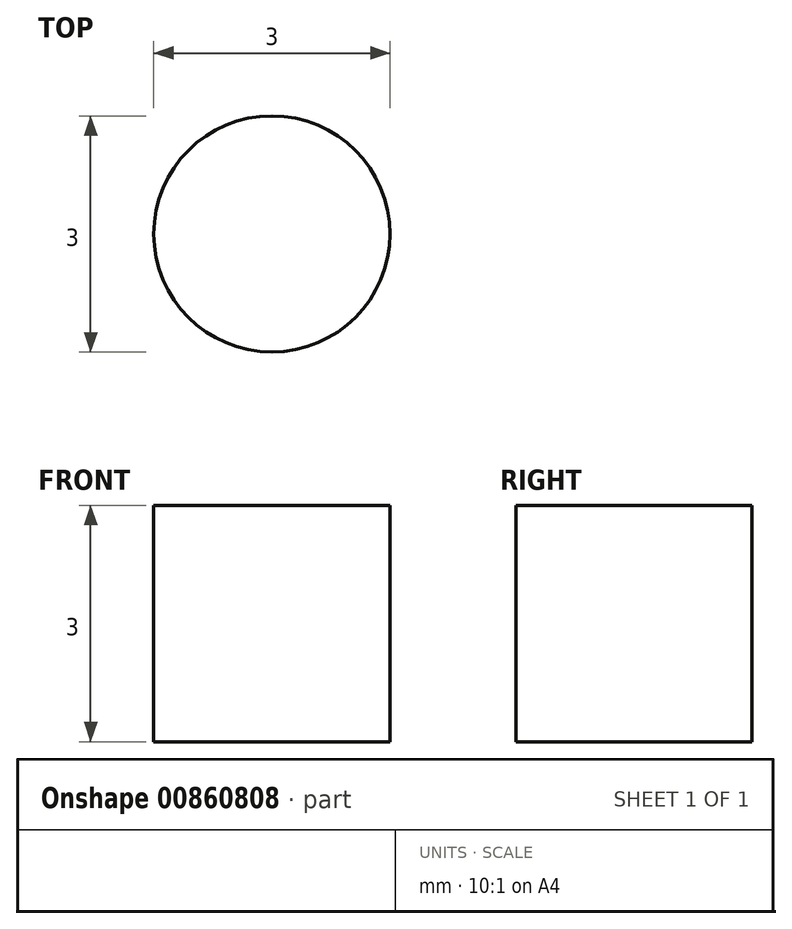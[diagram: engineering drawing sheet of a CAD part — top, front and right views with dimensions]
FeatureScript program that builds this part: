
annotation { "Feature Type Name" : "Feature", "Feature Type Description" : "" }
export const myFeature = defineFeature(function(context is Context, id is Id, definition is map)
    precondition{}
    {
        {
            var Q0;
            Q0=qCreatedBy(makeId("Top.planeOp"),FACE);
            var sketch = newSketch(context, id + "F0", { "sketchPlane" : qUnion([Q0])});
            skCircle(sketch, "E0", {"center": v(-15.25, 15.25) * mm, "radius": 1.5 * mm});
            skCircle(sketch, "E1", {"center": v(15.25, 15.25) * mm, "radius": 1.5 * mm});
            skCircle(sketch, "E2", {"center": v(-15.25, -15.25) * mm, "radius": 1.5 * mm});
            skCircle(sketch, "E3", {"center": v(15.25, -15.25) * mm, "radius": 1.5 * mm});
            skCircle(sketch, "E4", {"center": v(-12, 34.35) * mm, "radius": 1 * mm});
            skCircle(sketch, "E5", {"center": v(12, 34.35) * mm, "radius": 1 * mm});
            skCircle(sketch, "E6", {"center": v(-12, -26.35) * mm, "radius": 1 * mm});
            skCircle(sketch, "E7", {"center": v(-12, -34.35) * mm, "radius": 1 * mm});
            skCircle(sketch, "E8", {"center": v(12, -26.35) * mm, "radius": 1 * mm});
            skCircle(sketch, "E9", {"center": v(12, -34.35) * mm, "radius": 1 * mm});
            skCircle(sketch, "E10", {"center": v(-12, 26.35) * mm, "radius": 1 * mm});
            skCircle(sketch, "E11", {"center": v(12, 26.35) * mm, "radius": 1 * mm});
            skArc(sketch, "E12", {"start": v(9.25, 7) * mm, "mid": v(10.66, 6.41) * mm, "end": v(11.25, 5) * mm});
            skLineSegment(sketch, "E13", {"start": v(11.25, 5) * mm, "end": v(11.25, -5) * mm});
            skArc(sketch, "E14", {"start": v(11.25, -5) * mm, "mid": v(10.66, -6.41) * mm, "end": v(9.25, -7) * mm});
            skLineSegment(sketch, "E15", {"start": v(9.25, -7) * mm, "end": v(-9.25, -7) * mm});
            skArc(sketch, "E16", {"start": v(-9.25, -7) * mm, "mid": v(-10.66, -6.41) * mm, "end": v(-11.25, -5) * mm});
            skLineSegment(sketch, "E17", {"start": v(-11.25, -5) * mm, "end": v(-11.25, 5) * mm});
            skArc(sketch, "E18", {"start": v(-11.25, 5) * mm, "mid": v(-10.66, 6.41) * mm, "end": v(-9.25, 7) * mm});
            skLineSegment(sketch, "E19", {"start": v(-9.25, 7) * mm, "end": v(9.25, 7) * mm});
            skArc(sketch, "E20", {"start": v(8.75, 20.38) * mm, "mid": v(7.87, 18.26) * mm, "end": v(5.75, 17.38) * mm});
            skLineSegment(sketch, "E21", {"start": v(5.75, 17.38) * mm, "end": v(-5.75, 17.38) * mm});
            skArc(sketch, "E22", {"start": v(-5.75, 17.38) * mm, "mid": v(-7.87, 18.26) * mm, "end": v(-8.75, 20.38) * mm});
            skLineSegment(sketch, "E23", {"start": v(-8.75, 20.38) * mm, "end": v(-8.75, 30.5) * mm});
            skArc(sketch, "E24", {"start": v(-8.75, 30.5) * mm, "mid": v(-7.87, 32.62) * mm, "end": v(-5.75, 33.5) * mm});
            skLineSegment(sketch, "E25", {"start": v(-5.75, 33.5) * mm, "end": v(5.75, 33.5) * mm});
            skArc(sketch, "E26", {"start": v(5.75, 33.5) * mm, "mid": v(7.87, 32.62) * mm, "end": v(8.75, 30.5) * mm});
            skLineSegment(sketch, "E27", {"start": v(8.75, 30.5) * mm, "end": v(8.75, 20.38) * mm});
            skArc(sketch, "E28", {"start": v(-8.75, -30.74) * mm, "mid": v(-7.87, -32.86) * mm, "end": v(-5.75, -33.74) * mm});
            skLineSegment(sketch, "E29", {"start": v(-5.75, -33.74) * mm, "end": v(5.75, -33.74) * mm});
            skArc(sketch, "E30", {"start": v(5.75, -33.74) * mm, "mid": v(7.87, -32.86) * mm, "end": v(8.75, -30.74) * mm});
            skLineSegment(sketch, "E31", {"start": v(8.75, -30.74) * mm, "end": v(8.75, -20.38) * mm});
            skArc(sketch, "E32", {"start": v(8.75, -20.38) * mm, "mid": v(7.87, -18.26) * mm, "end": v(5.75, -17.38) * mm});
            skLineSegment(sketch, "E33", {"start": v(5.75, -17.38) * mm, "end": v(-5.75, -17.38) * mm});
            skArc(sketch, "E34", {"start": v(-5.75, -17.38) * mm, "mid": v(-7.87, -18.26) * mm, "end": v(-8.75, -20.38) * mm});
            skLineSegment(sketch, "E35", {"start": v(-8.75, -20.38) * mm, "end": v(-8.75, -30.74) * mm});
            skArc(sketch, "E36", {"start": v(39.96, 38.59) * mm, "mid": v(43.69, 41.27) * mm, "end": v(46.43, 44.96) * mm});
            skArc(sketch, "E37", {"start": v(46.43, 44.96) * mm, "mid": v(47.84, 47.05) * mm, "end": v(49.68, 48.78) * mm});
            skLineSegment(sketch, "E38", {"start": v(49.68, 48.78) * mm, "end": v(53.4, 51.6) * mm});
            skArc(sketch, "E39", {"start": v(53.4, 51.6) * mm, "mid": v(54.77, 52.32) * mm, "end": v(56.3, 52.6) * mm});
            skArc(sketch, "E40", {"start": v(56.3, 52.6) * mm, "mid": v(56.85, 52.6) * mm, "end": v(57.4, 52.58) * mm});
            skArc(sketch, "E41", {"start": v(57.4, 52.58) * mm, "mid": v(57.63, 52.62) * mm, "end": v(57.82, 52.76) * mm});
            skArc(sketch, "E42", {"start": v(57.82, 52.76) * mm, "mid": v(58, 52.9) * mm, "end": v(58.23, 52.94) * mm});
            skArc(sketch, "E43", {"start": v(58.23, 52.94) * mm, "mid": v(59, 52.87) * mm, "end": v(59.75, 52.73) * mm});
            skArc(sketch, "E44", {"start": v(59.75, 52.73) * mm, "mid": v(61.9, 52.01) * mm, "end": v(63.91, 50.95) * mm});
            skArc(sketch, "E45", {"start": v(63.91, 50.95) * mm, "mid": v(64.09, 50.75) * mm, "end": v(64.14, 50.49) * mm});
            skArc(sketch, "E46", {"start": v(64.14, 50.49) * mm, "mid": v(64.18, 50.24) * mm, "end": v(64.34, 50.04) * mm});
            skArc(sketch, "E47", {"start": v(64.34, 50.04) * mm, "mid": v(65.38, 49.18) * mm, "end": v(66.33, 48.22) * mm});
            skArc(sketch, "E48", {"start": v(66.33, 48.22) * mm, "mid": v(66.54, 48.08) * mm, "end": v(66.79, 48.06) * mm});
            skArc(sketch, "E49", {"start": v(66.79, 48.06) * mm, "mid": v(67.05, 48.03) * mm, "end": v(67.27, 47.87) * mm});
            skArc(sketch, "E50", {"start": v(67.27, 47.87) * mm, "mid": v(68.84, 45.3) * mm, "end": v(69.8, 42.45) * mm});
            skArc(sketch, "E51", {"start": v(69.8, 42.45) * mm, "mid": v(69.78, 42.19) * mm, "end": v(69.63, 41.97) * mm});
            skArc(sketch, "E52", {"start": v(69.63, 41.97) * mm, "mid": v(69.49, 41.76) * mm, "end": v(69.46, 41.51) * mm});
            skArc(sketch, "E53", {"start": v(69.46, 41.51) * mm, "mid": v(69.59, 40.17) * mm, "end": v(69.58, 38.82) * mm});
            skArc(sketch, "E54", {"start": v(69.58, 38.82) * mm, "mid": v(69.62, 38.57) * mm, "end": v(69.79, 38.38) * mm});
            skArc(sketch, "E55", {"start": v(69.79, 38.38) * mm, "mid": v(69.96, 38.17) * mm, "end": v(70, 37.9) * mm});
            skArc(sketch, "E56", {"start": v(70, 37.9) * mm, "mid": v(69.65, 36.14) * mm, "end": v(69.07, 34.43) * mm});
            skArc(sketch, "E57", {"start": v(69.07, 34.43) * mm, "mid": v(68.5, 33.3) * mm, "end": v(67.75, 32.28) * mm});
            skArc(sketch, "E58", {"start": v(67.75, 32.28) * mm, "mid": v(67.6, 32.16) * mm, "end": v(67.42, 32.1) * mm});
            skArc(sketch, "E59", {"start": v(67.42, 32.1) * mm, "mid": v(67.23, 32.04) * mm, "end": v(67.08, 31.9) * mm});
            skArc(sketch, "E60", {"start": v(67.08, 31.9) * mm, "mid": v(67, 31.8) * mm, "end": v(66.94, 31.71) * mm});
            skArc(sketch, "E61", {"start": v(66.94, 31.71) * mm, "mid": v(65.82, 30.64) * mm, "end": v(64.42, 29.97) * mm});
            skLineSegment(sketch, "E62", {"start": v(64.42, 29.97) * mm, "end": v(59.96, 28.6) * mm});
            skArc(sketch, "E63", {"start": v(59.96, 28.6) * mm, "mid": v(57.48, 28.13) * mm, "end": v(54.96, 28.22) * mm});
            skArc(sketch, "E64", {"start": v(54.96, 28.22) * mm, "mid": v(50.37, 28.17) * mm, "end": v(46, 26.74) * mm});
            skLineSegment(sketch, "E65", {"start": v(46, 26.74) * mm, "end": v(23.16, 15.1) * mm});
            skArc(sketch, "E66", {"start": v(23.16, 15.1) * mm, "mid": v(19.58, 11.78) * mm, "end": v(18.25, 7.08) * mm});
            skLineSegment(sketch, "E67", {"start": v(18.25, 7.08) * mm, "end": v(18.25, -7.08) * mm});
            skArc(sketch, "E68", {"start": v(18.25, -7.08) * mm, "mid": v(19.58, -11.78) * mm, "end": v(23.16, -15.1) * mm});
            skLineSegment(sketch, "E69", {"start": v(23.16, -15.1) * mm, "end": v(46, -26.74) * mm});
            skArc(sketch, "E70", {"start": v(46, -26.74) * mm, "mid": v(50.37, -28.17) * mm, "end": v(54.96, -28.22) * mm});
            skArc(sketch, "E71", {"start": v(54.96, -28.22) * mm, "mid": v(57.48, -28.13) * mm, "end": v(59.96, -28.6) * mm});
            skLineSegment(sketch, "E72", {"start": v(59.96, -28.6) * mm, "end": v(64.42, -29.97) * mm});
            skArc(sketch, "E73", {"start": v(64.42, -29.97) * mm, "mid": v(65.82, -30.64) * mm, "end": v(66.94, -31.71) * mm});
            skArc(sketch, "E74", {"start": v(66.94, -31.71) * mm, "mid": v(67, -31.8) * mm, "end": v(67.08, -31.9) * mm});
            skArc(sketch, "E75", {"start": v(67.08, -31.9) * mm, "mid": v(67.23, -32.04) * mm, "end": v(67.42, -32.1) * mm});
            skArc(sketch, "E76", {"start": v(67.42, -32.1) * mm, "mid": v(67.6, -32.16) * mm, "end": v(67.75, -32.28) * mm});
            skArc(sketch, "E77", {"start": v(67.75, -32.28) * mm, "mid": v(68.5, -33.3) * mm, "end": v(69.07, -34.43) * mm});
            skArc(sketch, "E78", {"start": v(69.07, -34.43) * mm, "mid": v(69.65, -36.14) * mm, "end": v(70, -37.9) * mm});
            skArc(sketch, "E79", {"start": v(70, -37.9) * mm, "mid": v(69.96, -38.17) * mm, "end": v(69.79, -38.38) * mm});
            skArc(sketch, "E80", {"start": v(69.79, -38.38) * mm, "mid": v(69.62, -38.57) * mm, "end": v(69.58, -38.82) * mm});
            skArc(sketch, "E81", {"start": v(69.58, -38.82) * mm, "mid": v(69.59, -40.17) * mm, "end": v(69.46, -41.51) * mm});
            skArc(sketch, "E82", {"start": v(69.46, -41.51) * mm, "mid": v(69.49, -41.76) * mm, "end": v(69.63, -41.97) * mm});
            skArc(sketch, "E83", {"start": v(69.63, -41.97) * mm, "mid": v(69.78, -42.19) * mm, "end": v(69.8, -42.45) * mm});
            skArc(sketch, "E84", {"start": v(69.8, -42.45) * mm, "mid": v(68.84, -45.3) * mm, "end": v(67.27, -47.87) * mm});
            skArc(sketch, "E85", {"start": v(67.27, -47.87) * mm, "mid": v(67.05, -48.03) * mm, "end": v(66.79, -48.06) * mm});
            skArc(sketch, "E86", {"start": v(66.79, -48.06) * mm, "mid": v(66.54, -48.08) * mm, "end": v(66.33, -48.22) * mm});
            skArc(sketch, "E87", {"start": v(66.33, -48.22) * mm, "mid": v(65.38, -49.18) * mm, "end": v(64.34, -50.04) * mm});
            skArc(sketch, "E88", {"start": v(64.34, -50.04) * mm, "mid": v(64.18, -50.24) * mm, "end": v(64.14, -50.49) * mm});
            skArc(sketch, "E89", {"start": v(64.14, -50.49) * mm, "mid": v(64.09, -50.75) * mm, "end": v(63.91, -50.95) * mm});
            skArc(sketch, "E90", {"start": v(63.91, -50.95) * mm, "mid": v(61.9, -52.01) * mm, "end": v(59.75, -52.73) * mm});
            skArc(sketch, "E91", {"start": v(59.75, -52.73) * mm, "mid": v(59, -52.87) * mm, "end": v(58.23, -52.94) * mm});
            skArc(sketch, "E92", {"start": v(58.23, -52.94) * mm, "mid": v(58, -52.9) * mm, "end": v(57.82, -52.76) * mm});
            skArc(sketch, "E93", {"start": v(57.82, -52.76) * mm, "mid": v(57.63, -52.62) * mm, "end": v(57.4, -52.58) * mm});
            skArc(sketch, "E94", {"start": v(57.4, -52.58) * mm, "mid": v(56.85, -52.6) * mm, "end": v(56.3, -52.6) * mm});
            skArc(sketch, "E95", {"start": v(56.3, -52.6) * mm, "mid": v(54.77, -52.32) * mm, "end": v(53.4, -51.6) * mm});
            skLineSegment(sketch, "E96", {"start": v(53.4, -51.6) * mm, "end": v(49.68, -48.78) * mm});
            skArc(sketch, "E97", {"start": v(49.68, -48.78) * mm, "mid": v(47.84, -47.05) * mm, "end": v(46.43, -44.96) * mm});
            skArc(sketch, "E98", {"start": v(46.43, -44.96) * mm, "mid": v(43.69, -41.27) * mm, "end": v(39.96, -38.59) * mm});
            skLineSegment(sketch, "E99", {"start": v(39.96, -38.59) * mm, "end": v(24.22, -30.57) * mm});
            skArc(sketch, "E100", {"start": v(24.22, -30.57) * mm, "mid": v(18.37, -30.8) * mm, "end": v(15.5, -35.91) * mm});
            skLineSegment(sketch, "E101", {"start": v(15.5, -35.91) * mm, "end": v(15.5, -40.74) * mm});
            skLineSegment(sketch, "E102", {"start": v(15.5, -40.74) * mm, "end": v(-15.5, -40.74) * mm});
            skLineSegment(sketch, "E103", {"start": v(-15.5, -40.74) * mm, "end": v(-15.5, -35.91) * mm});
            skArc(sketch, "E104", {"start": v(-15.5, -35.91) * mm, "mid": v(-18.37, -30.8) * mm, "end": v(-24.22, -30.57) * mm});
            skLineSegment(sketch, "E105", {"start": v(-24.22, -30.57) * mm, "end": v(-39.96, -38.59) * mm});
            skArc(sketch, "E106", {"start": v(-39.96, -38.59) * mm, "mid": v(-43.69, -41.27) * mm, "end": v(-46.43, -44.96) * mm});
            skArc(sketch, "E107", {"start": v(-46.43, -44.96) * mm, "mid": v(-47.84, -47.05) * mm, "end": v(-49.68, -48.78) * mm});
            skLineSegment(sketch, "E108", {"start": v(-49.68, -48.78) * mm, "end": v(-53.4, -51.6) * mm});
            skArc(sketch, "E109", {"start": v(-53.4, -51.6) * mm, "mid": v(-54.77, -52.32) * mm, "end": v(-56.3, -52.6) * mm});
            skArc(sketch, "E110", {"start": v(-56.3, -52.6) * mm, "mid": v(-56.85, -52.6) * mm, "end": v(-57.4, -52.58) * mm});
            skArc(sketch, "E111", {"start": v(-57.4, -52.58) * mm, "mid": v(-57.63, -52.62) * mm, "end": v(-57.82, -52.76) * mm});
            skArc(sketch, "E112", {"start": v(-57.82, -52.76) * mm, "mid": v(-58, -52.9) * mm, "end": v(-58.23, -52.94) * mm});
            skArc(sketch, "E113", {"start": v(-58.23, -52.94) * mm, "mid": v(-59, -52.87) * mm, "end": v(-59.75, -52.73) * mm});
            skArc(sketch, "E114", {"start": v(-59.75, -52.73) * mm, "mid": v(-61.9, -52.01) * mm, "end": v(-63.91, -50.95) * mm});
            skArc(sketch, "E115", {"start": v(-63.91, -50.95) * mm, "mid": v(-64.09, -50.75) * mm, "end": v(-64.14, -50.49) * mm});
            skArc(sketch, "E116", {"start": v(-64.14, -50.49) * mm, "mid": v(-64.18, -50.24) * mm, "end": v(-64.34, -50.04) * mm});
            skArc(sketch, "E117", {"start": v(-64.34, -50.04) * mm, "mid": v(-65.38, -49.18) * mm, "end": v(-66.33, -48.22) * mm});
            skArc(sketch, "E118", {"start": v(-66.33, -48.22) * mm, "mid": v(-66.54, -48.08) * mm, "end": v(-66.79, -48.06) * mm});
            skArc(sketch, "E119", {"start": v(-66.79, -48.06) * mm, "mid": v(-67.05, -48.03) * mm, "end": v(-67.27, -47.87) * mm});
            skArc(sketch, "E120", {"start": v(-67.27, -47.87) * mm, "mid": v(-68.84, -45.3) * mm, "end": v(-69.8, -42.45) * mm});
            skArc(sketch, "E121", {"start": v(-69.8, -42.45) * mm, "mid": v(-69.78, -42.19) * mm, "end": v(-69.63, -41.97) * mm});
            skArc(sketch, "E122", {"start": v(-69.63, -41.97) * mm, "mid": v(-69.49, -41.76) * mm, "end": v(-69.46, -41.51) * mm});
            skArc(sketch, "E123", {"start": v(-69.46, -41.51) * mm, "mid": v(-69.59, -40.17) * mm, "end": v(-69.58, -38.82) * mm});
            skArc(sketch, "E124", {"start": v(-69.58, -38.82) * mm, "mid": v(-69.62, -38.57) * mm, "end": v(-69.79, -38.38) * mm});
            skArc(sketch, "E125", {"start": v(-69.79, -38.38) * mm, "mid": v(-69.96, -38.17) * mm, "end": v(-70, -37.9) * mm});
            skArc(sketch, "E126", {"start": v(-70, -37.9) * mm, "mid": v(-69.65, -36.14) * mm, "end": v(-69.07, -34.43) * mm});
            skArc(sketch, "E127", {"start": v(-69.07, -34.43) * mm, "mid": v(-68.5, -33.3) * mm, "end": v(-67.75, -32.28) * mm});
            skArc(sketch, "E128", {"start": v(-67.75, -32.28) * mm, "mid": v(-67.6, -32.16) * mm, "end": v(-67.42, -32.1) * mm});
            skArc(sketch, "E129", {"start": v(-67.42, -32.1) * mm, "mid": v(-67.23, -32.04) * mm, "end": v(-67.08, -31.9) * mm});
            skArc(sketch, "E130", {"start": v(-67.08, -31.9) * mm, "mid": v(-67, -31.8) * mm, "end": v(-66.94, -31.71) * mm});
            skArc(sketch, "E131", {"start": v(-66.94, -31.71) * mm, "mid": v(-65.82, -30.64) * mm, "end": v(-64.42, -29.97) * mm});
            skLineSegment(sketch, "E132", {"start": v(-64.42, -29.97) * mm, "end": v(-59.96, -28.6) * mm});
            skArc(sketch, "E133", {"start": v(-59.96, -28.6) * mm, "mid": v(-57.48, -28.13) * mm, "end": v(-54.96, -28.22) * mm});
            skArc(sketch, "E134", {"start": v(-54.96, -28.22) * mm, "mid": v(-50.37, -28.17) * mm, "end": v(-46, -26.74) * mm});
            skLineSegment(sketch, "E135", {"start": v(-46, -26.74) * mm, "end": v(-23.16, -15.1) * mm});
            skArc(sketch, "E136", {"start": v(-23.16, -15.1) * mm, "mid": v(-19.58, -11.78) * mm, "end": v(-18.25, -7.08) * mm});
            skLineSegment(sketch, "E137", {"start": v(-18.25, -7.08) * mm, "end": v(-18.25, 7.08) * mm});
            skArc(sketch, "E138", {"start": v(-18.25, 7.08) * mm, "mid": v(-19.58, 11.78) * mm, "end": v(-23.16, 15.1) * mm});
            skLineSegment(sketch, "E139", {"start": v(-23.16, 15.1) * mm, "end": v(-46, 26.74) * mm});
            skArc(sketch, "E140", {"start": v(-46, 26.74) * mm, "mid": v(-50.37, 28.17) * mm, "end": v(-54.96, 28.22) * mm});
            skArc(sketch, "E141", {"start": v(-54.96, 28.22) * mm, "mid": v(-57.48, 28.13) * mm, "end": v(-59.96, 28.6) * mm});
            skLineSegment(sketch, "E142", {"start": v(-59.96, 28.6) * mm, "end": v(-64.42, 29.97) * mm});
            skArc(sketch, "E143", {"start": v(-64.42, 29.97) * mm, "mid": v(-65.82, 30.64) * mm, "end": v(-66.94, 31.71) * mm});
            skArc(sketch, "E144", {"start": v(-66.94, 31.71) * mm, "mid": v(-67, 31.8) * mm, "end": v(-67.08, 31.9) * mm});
            skArc(sketch, "E145", {"start": v(-67.08, 31.9) * mm, "mid": v(-67.23, 32.04) * mm, "end": v(-67.42, 32.1) * mm});
            skArc(sketch, "E146", {"start": v(-67.42, 32.1) * mm, "mid": v(-67.6, 32.16) * mm, "end": v(-67.75, 32.28) * mm});
            skArc(sketch, "E147", {"start": v(-67.75, 32.28) * mm, "mid": v(-68.5, 33.3) * mm, "end": v(-69.07, 34.43) * mm});
            skArc(sketch, "E148", {"start": v(-69.07, 34.43) * mm, "mid": v(-69.65, 36.14) * mm, "end": v(-70, 37.9) * mm});
            skArc(sketch, "E149", {"start": v(-70, 37.9) * mm, "mid": v(-69.96, 38.17) * mm, "end": v(-69.79, 38.38) * mm});
            skArc(sketch, "E150", {"start": v(-69.79, 38.38) * mm, "mid": v(-69.62, 38.57) * mm, "end": v(-69.58, 38.82) * mm});
            skArc(sketch, "E151", {"start": v(-69.58, 38.82) * mm, "mid": v(-69.59, 40.17) * mm, "end": v(-69.46, 41.51) * mm});
            skArc(sketch, "E152", {"start": v(-69.46, 41.51) * mm, "mid": v(-69.49, 41.76) * mm, "end": v(-69.63, 41.97) * mm});
            skArc(sketch, "E153", {"start": v(-69.63, 41.97) * mm, "mid": v(-69.78, 42.19) * mm, "end": v(-69.8, 42.45) * mm});
            skArc(sketch, "E154", {"start": v(-69.8, 42.45) * mm, "mid": v(-68.84, 45.3) * mm, "end": v(-67.27, 47.87) * mm});
            skArc(sketch, "E155", {"start": v(-67.27, 47.87) * mm, "mid": v(-67.05, 48.03) * mm, "end": v(-66.79, 48.06) * mm});
            skArc(sketch, "E156", {"start": v(-66.79, 48.06) * mm, "mid": v(-66.54, 48.08) * mm, "end": v(-66.33, 48.22) * mm});
            skArc(sketch, "E157", {"start": v(-66.33, 48.22) * mm, "mid": v(-65.38, 49.18) * mm, "end": v(-64.34, 50.04) * mm});
            skArc(sketch, "E158", {"start": v(-64.34, 50.04) * mm, "mid": v(-64.18, 50.24) * mm, "end": v(-64.14, 50.49) * mm});
            skArc(sketch, "E159", {"start": v(-64.14, 50.49) * mm, "mid": v(-64.09, 50.75) * mm, "end": v(-63.91, 50.95) * mm});
            skArc(sketch, "E160", {"start": v(-63.91, 50.95) * mm, "mid": v(-61.9, 52.01) * mm, "end": v(-59.75, 52.73) * mm});
            skArc(sketch, "E161", {"start": v(-59.75, 52.73) * mm, "mid": v(-59, 52.87) * mm, "end": v(-58.23, 52.94) * mm});
            skArc(sketch, "E162", {"start": v(-58.23, 52.94) * mm, "mid": v(-58, 52.9) * mm, "end": v(-57.82, 52.76) * mm});
            skArc(sketch, "E163", {"start": v(-57.82, 52.76) * mm, "mid": v(-57.63, 52.62) * mm, "end": v(-57.4, 52.58) * mm});
            skArc(sketch, "E164", {"start": v(-57.4, 52.58) * mm, "mid": v(-56.85, 52.6) * mm, "end": v(-56.3, 52.6) * mm});
            skArc(sketch, "E165", {"start": v(-56.3, 52.6) * mm, "mid": v(-54.77, 52.32) * mm, "end": v(-53.4, 51.6) * mm});
            skLineSegment(sketch, "E166", {"start": v(-53.4, 51.6) * mm, "end": v(-49.68, 48.78) * mm});
            skArc(sketch, "E167", {"start": v(-49.68, 48.78) * mm, "mid": v(-47.84, 47.05) * mm, "end": v(-46.43, 44.96) * mm});
            skArc(sketch, "E168", {"start": v(-46.43, 44.96) * mm, "mid": v(-43.69, 41.27) * mm, "end": v(-39.96, 38.59) * mm});
            skLineSegment(sketch, "E169", {"start": v(-39.96, 38.59) * mm, "end": v(-24.22, 30.57) * mm});
            skArc(sketch, "E170", {"start": v(-24.22, 30.57) * mm, "mid": v(-18.37, 30.8) * mm, "end": v(-15.5, 35.91) * mm});
            skLineSegment(sketch, "E171", {"start": v(-15.5, 35.91) * mm, "end": v(-15.5, 37.85) * mm});
            skLineSegment(sketch, "E172", {"start": v(-15.5, 37.85) * mm, "end": v(15.5, 37.85) * mm});
            skLineSegment(sketch, "E173", {"start": v(15.5, 37.85) * mm, "end": v(15.5, 35.91) * mm});
            skArc(sketch, "E174", {"start": v(15.5, 35.91) * mm, "mid": v(18.37, 30.8) * mm, "end": v(24.22, 30.57) * mm});
            skLineSegment(sketch, "E175", {"start": v(24.22, 30.57) * mm, "end": v(39.96, 38.59) * mm});
            skCircle(sketch, "E176", {"center": v(-10, 10) * mm, "radius": 1.6 * mm});
            skCircle(sketch, "E177", {"center": v(-10, -10) * mm, "radius": 1.6 * mm});
            skCircle(sketch, "E178", {"center": v(10, -10) * mm, "radius": 1.6 * mm});
            skCircle(sketch, "E179", {"center": v(10, 10) * mm, "radius": 1.6 * mm});
            skCircle(sketch, "E180", {"center": v(-56.6, 39.6) * mm, "radius": 3.25 * mm});
            skCircle(sketch, "E181", {"center": v(-62.3, 37.75) * mm, "radius": 1.05 * mm});
            skCircle(sketch, "E182", {"center": v(-54.75, 33.9) * mm, "radius": 1.05 * mm});
            skCircle(sketch, "E183", {"center": v(-50.9, 41.45) * mm, "radius": 1.05 * mm});
            skCircle(sketch, "E184", {"center": v(-58.45, 45.3) * mm, "radius": 1.05 * mm});
            skCircle(sketch, "E185", {"center": v(56.6, 39.6) * mm, "radius": 3.25 * mm});
            skCircle(sketch, "E186", {"center": v(62.3, 37.75) * mm, "radius": 1.05 * mm});
            skCircle(sketch, "E187", {"center": v(54.75, 33.9) * mm, "radius": 1.05 * mm});
            skCircle(sketch, "E188", {"center": v(50.9, 41.45) * mm, "radius": 1.05 * mm});
            skCircle(sketch, "E189", {"center": v(58.45, 45.3) * mm, "radius": 1.05 * mm});
            skCircle(sketch, "E190", {"center": v(-56.6, -39.6) * mm, "radius": 3.25 * mm});
            skCircle(sketch, "E191", {"center": v(-62.3, -37.75) * mm, "radius": 1.05 * mm});
            skCircle(sketch, "E192", {"center": v(-54.75, -33.9) * mm, "radius": 1.05 * mm});
            skCircle(sketch, "E193", {"center": v(-50.9, -41.45) * mm, "radius": 1.05 * mm});
            skCircle(sketch, "E194", {"center": v(-58.45, -45.3) * mm, "radius": 1.05 * mm});
            skCircle(sketch, "E195", {"center": v(56.6, -39.6) * mm, "radius": 3.25 * mm});
            skCircle(sketch, "E196", {"center": v(62.3, -37.75) * mm, "radius": 1.05 * mm});
            skCircle(sketch, "E197", {"center": v(54.75, -33.9) * mm, "radius": 1.05 * mm});
            skCircle(sketch, "E198", {"center": v(50.9, -41.45) * mm, "radius": 1.05 * mm});
            skCircle(sketch, "E199", {"center": v(58.45, -45.3) * mm, "radius": 1.05 * mm});
            skSolve(sketch);
        }
        {
            var Q0;
            Q0=makeQuery(id+"F0.imprint","IMPRINT",FACE,{"disambiguationData":[TD([[makeQuery(id+"F0.imprint","IMPRINT",EDGE,{"derivedFrom":sQuery(id+"F0.wireOp",EDGE,"E0")}),1.0]])]});
            extrude(context, id + "F1", {"entities" : qUnion([Q0]), "depth" : 3 * mm, "offsetDistance" : 25 * mm});
        }
    });
